# Revit family: Наружный блок 2х трубная система VRF системы
name_source: partatom
category: Mechanical Equipment
revit_build: Autodesk Revit 2016 (Build: 20150506_1715(x64)
units: mm (PartAtom-declared; Revit-internal decimal feet)

## family parameters
Cut with Voids When Loaded = No
Host = Face
Part Type = Normal
Room Calculation Point = No
Round Connector Dimension = Use Diameter
Shared = No

## types (6) — shared parameters
Default Elevation = 1219.2 mm  [stored 4 ft]
Высота = 1720 mm
Глубина = 750 mm  [stored 2.46063 ft]
Наименование = Наружный блок с рекуперацией VRF-системы
Производитель = Electrolux
Таблица модель = Модель
Таблица наименование = Наименование
Таблица параметров = Таблица параметров
Таблица расход воздуха = Расход воздуха
Таблица тип хладагента = Тип хладагента
Таблица уровень звукового давления = Уровень звукового давления
Таблица электропитание = Электропитание
Тип хладогента = R410А
Фаза = 3
Частота сети = 50 Hz
Эл. питание(коннектор) = 380 V
Электропитание, (В) = 380

## per-type parameters (varying)
| type | SCOP, (кВт/кВт) | SEER, (кВт/кВт) | Артикул | Вес | Диаметр газовой трубы | Диаметр жидкостной трубы | Максимальная потребляемая мощность_Нагрев | Максимальная потребляемая мощность_Охлаждение | Максимальное кол-во подключаемых внутренних блоков, шт | Максимальный ток | Масса хладагента | Расход воздуха, (м.куб/ч) | Теплопроизводительность | Уровень звукового давления, (Дб(А)) | Холодопроизводительность | Ширина | Эффективная потребляемая мощность_Нагрев | Эффективная потребляемая мощность_Охлаждение |
| ESVMO-SF-224-R | 8 | 7.4 | 1040278 | 210.00 kg | 19.05 mm  [stored 0.0625 ft] | 9.53 mm | 5.23 kW | 5.09 kW | 13 | 13 A | 6.50 kg | 9300 | 25.00 kW | 56-54-52 | 22.40 kW | 950 mm  [stored 3.1168 ft] | 3.14 kW | 3.05 kW |
| ESVMO-SF-280-R | 7.5 | 6.8 | 1040279 | 212.00 kg | 22.2 mm  [stored 0.0728346 ft] | 9.53 mm | 6.98 kW | 6.89 kW | 16 | 17 A | 6.50 kg | 10200 | 31.50 kW | 56-54-53 | 28.00 kW | 950 mm  [stored 3.1168 ft] | 4.19 kW | 4.13 kW |
| ESVMO-SF-335-R | 6.9 | 6.1 | 1040280 | 215.00 kg | 25.4 mm  [stored 0.0833333 ft] | 12.7 mm  [stored 0.0416667 ft] | 9.11 kW | 9.16 kW | 19 | 23 A | 9.90 kg | 10500 | 37.50 kW | 58-56-54 | 33.50 kW | 950 mm  [stored 3.1168 ft] | 5.46 kW | 5.50 kW |
| ESVMO-SF-400-R | 7.6 | 6.2 | 1040281 | 298.00 kg | 25.4 mm  [stored 0.0833333 ft] | 12.7 mm  [stored 0.0416667 ft] | 10.17 kW | 11.03 kW | 23 | 28 A | 9.90 kg | 11700 | 45.00 kW | 60-58-56 | 40.00 kW | 1210 mm  [stored 3.96982 ft] | 6.10 kW | 6.62 kW |
| ESVMO-SF-450-R | 7.6 | 6.3 | 1040282 | 312.00 kg | 28.6 mm  [stored 0.093832 ft] | 12.7 mm  [stored 0.0416667 ft] | 11.34 kW | 12.37 kW | 26 | 31 A | 10.50 kg | 11700 | 50.00 kW | 60-58-56 | 45.00 kW | 1210 mm  [stored 3.96982 ft] | 6.80 kW | 7.42 kW |
| ESVMO-SF-504-R | 7.1 | 5.9 | 1040283 | 318.00 kg | 28.6 mm  [stored 0.093832 ft] | 15.88 mm  [stored 0.0520997 ft] | 13.77 kW | 14.94 kW | 26 | 33 A | 10.50 kg | 11700 | 56.00 kW | 61-59-57 | 50.00 kW | 1210 mm  [stored 3.96982 ft] | 8.26 kW | 8.96 kW |

note: column(s) folded — value = type name in every type: Модель

note: [stored X ft] marks values corroborated as IEEE doubles in the binary element streams (Revit-internal decimal feet)
